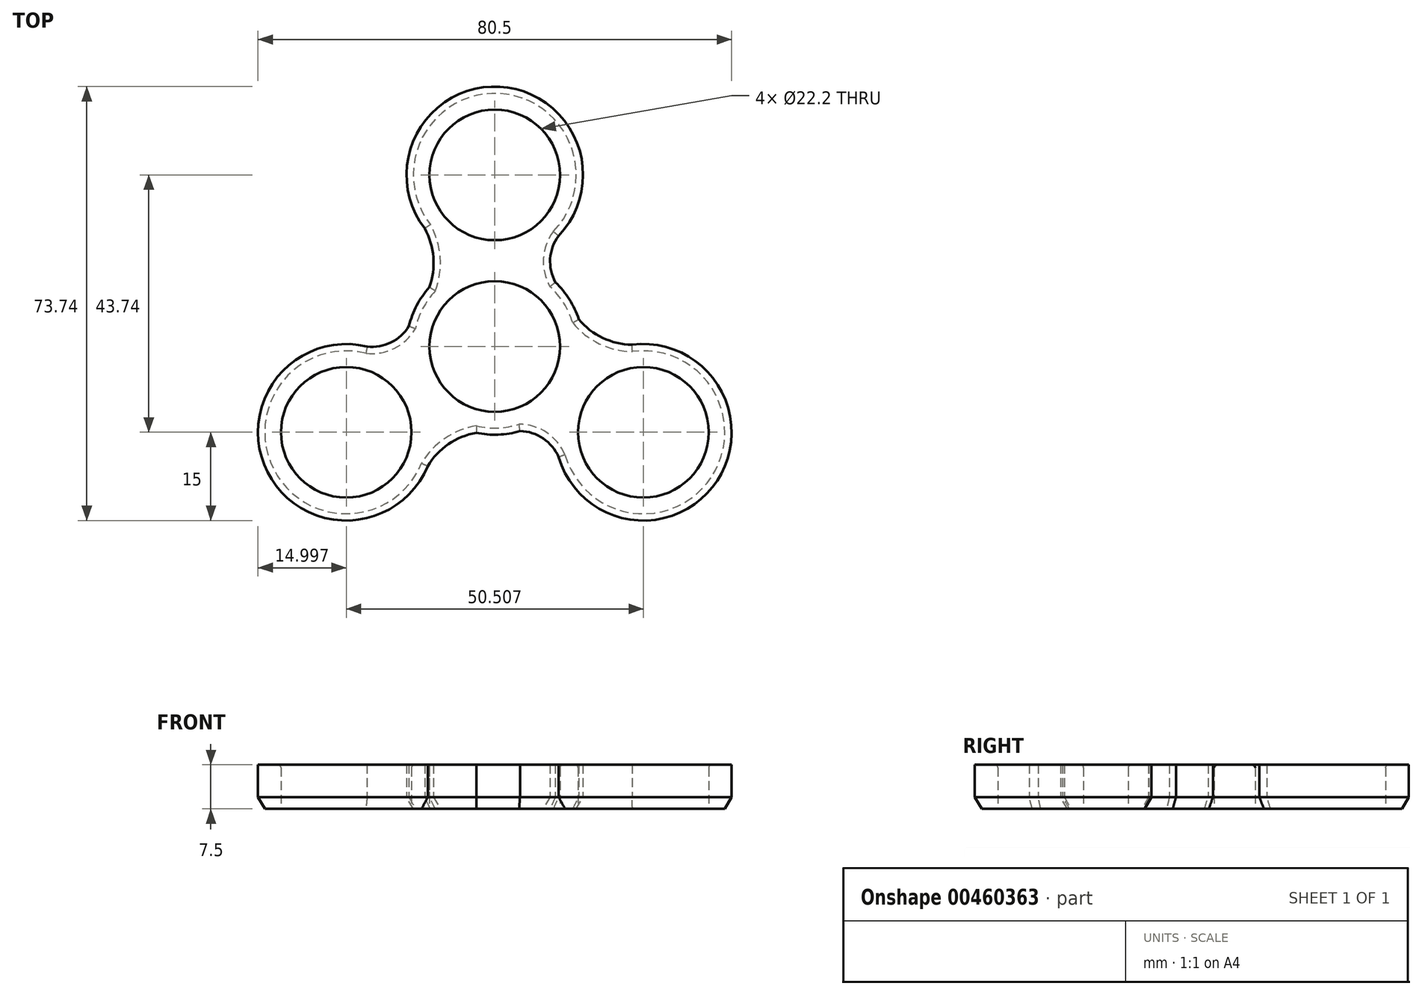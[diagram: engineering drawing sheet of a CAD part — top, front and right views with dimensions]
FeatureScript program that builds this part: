
annotation { "Feature Type Name" : "Feature", "Feature Type Description" : "" }
export const myFeature = defineFeature(function(context is Context, id is Id, definition is map)
    precondition{}
    {
        {
            var Q0;
            Q0=qCreatedBy(makeId("Top.planeOp"),FACE);
            var sketch = newSketch(context, id + "F0", { "sketchPlane" : qUnion([Q0])});
            skCircle(sketch, "E0", {"center": v(0, 0) * mm, "radius": 11.1 * mm});
            skCircle(sketch, "E1", {"center": v(0, 0) * mm, "radius": 15 * mm});
            skCircle(sketch, "E2", {"center": v(0, 29.16) * mm, "radius": 11.1 * mm});
            skCircle(sketch, "E3", {"center": v(0, 29.16) * mm, "radius": 15 * mm});
            skArc(sketch, "E4", {"start": v(-11.13, 10.06) * mm, "mid": v(-10.43, 15.14) * mm, "end": v(-11.92, 20.05) * mm});
            skArc(sketch, "E5", {"start": v(10.85, 18.8) * mm, "mid": v(9.41, 14.93) * mm, "end": v(10.3, 10.9) * mm});
            skCircle(sketch, "E6.1.0", {"center": v(-25.25, -14.58) * mm, "radius": 15 * mm});
            skCircle(sketch, "E6.1.1", {"center": v(-25.25, -14.58) * mm, "radius": 11.1 * mm});
            skArc(sketch, "E6.1.2", {"start": v(-3.15, -14.67) * mm, "mid": v(-7.9, -16.6) * mm, "end": v(-11.4, -20.35) * mm});
            skArc(sketch, "E6.1.3", {"start": v(-21.7, 0) * mm, "mid": v(-17.64, 0.69) * mm, "end": v(-14.6, 3.47) * mm});
            skCircle(sketch, "E6.2.0", {"center": v(25.25, -14.58) * mm, "radius": 15 * mm});
            skCircle(sketch, "E6.2.1", {"center": v(25.25, -14.58) * mm, "radius": 11.1 * mm});
            skArc(sketch, "E6.2.2", {"start": v(14.27, 4.6) * mm, "mid": v(18.33, 1.47) * mm, "end": v(23.33, 0.3) * mm});
            skArc(sketch, "E6.2.3", {"start": v(10.86, -18.8) * mm, "mid": v(8.22, -15.62) * mm, "end": v(4.29, -14.37) * mm});
            skSolve(sketch);
        }
        {
            var Q0;
            Q0 = qSketchRegion(id + "F0", true);
            extrude(context, id + "F1", {"entities" : qUnion([Q0]), "depth" : 7.5 * mm, "offsetDistance" : 25 * mm});
        }
        {
            var Q0;
            {var subQ0=sQuery(id+"F0.wireOp",EDGE,"E6.2.0");var subQ1=sQuery(id+"F0.wireOp",EDGE,"E1");var subQ2=makeQuery(id+"F0.imprint","INTERSECT",VERTEX,{"disambiguationData":[OD(0.0)],"derivedFrom":[subQ1,subQ0]});Q0=makeQuery(id+"F0.imprint","IMPRINT",FACE,{"disambiguationData":[TD([[makeQuery(id+"F0.imprint","IMPRINT",EDGE,{"disambiguationData":[TD([[subQ2,-1.0]])],"derivedFrom":subQ1}),1.0]])]});}
            var Q1;
            {var subQ0=sQuery(id+"F0.wireOp",EDGE,"E6.1.0");var subQ1=sQuery(id+"F0.wireOp",EDGE,"E1");var subQ2=makeQuery(id+"F0.imprint","INTERSECT",VERTEX,{"disambiguationData":[OD(0.0)],"derivedFrom":[subQ1,subQ0]});Q1=makeQuery(id+"F0.imprint","IMPRINT",FACE,{"disambiguationData":[TD([[makeQuery(id+"F0.imprint","IMPRINT",EDGE,{"disambiguationData":[TD([[subQ2,-1.0]])],"derivedFrom":subQ1}),1.0]])]});}
            var Q2;
            {var subQ0=sQuery(id+"F0.wireOp",EDGE,"E3");var subQ1=sQuery(id+"F0.wireOp",EDGE,"E1");var subQ2=makeQuery(id+"F0.imprint","INTERSECT",VERTEX,{"disambiguationData":[OD(0.0)],"derivedFrom":[subQ1,subQ0]});Q2=makeQuery(id+"F0.imprint","IMPRINT",FACE,{"disambiguationData":[TD([[makeQuery(id+"F0.imprint","IMPRINT",EDGE,{"disambiguationData":[TD([[subQ2,-1.0]])],"derivedFrom":subQ1}),1.0]])]});}
            extrude(context, id + "F2", {"entities" : qUnion([Q0, Q1, Q2]), "operationType" : NewBodyOperationType.ADD, "depth" : 7.5 * mm, "offsetDistance" : 25 * mm});
        }
        {
            var Q0;
            Q0=makeQuery(id+"F1.opExtrude","CAP_EDGE",EDGE,{"disambiguationData":[OSD([sQuery(id+"F0.wireOp",EDGE,"E2")])],"isStart":false});
            var Q1;
            Q1=makeQuery(id+"F1.opExtrude","CAP_EDGE",EDGE,{"disambiguationData":[OSD([sQuery(id+"F0.wireOp",EDGE,"E0")])],"isStart":false});
            var Q2;
            Q2=makeQuery(id+"F1.opExtrude","CAP_EDGE",EDGE,{"disambiguationData":[OSD([sQuery(id+"F0.wireOp",EDGE,"E6.2.1")])],"isStart":false});
            var Q3;
            Q3=makeQuery(id+"F1.opExtrude","CAP_EDGE",EDGE,{"disambiguationData":[OSD([sQuery(id+"F0.wireOp",EDGE,"E6.1.1")])],"isStart":false});
            fillet(context, id + "F3", {"entities" : qUnion([Q0, Q1, Q2, Q3]), "radius" : 0.5 * mm, "tangentPropagation" : true, "allowEdgeOverflow" : false});
        }
        {
            var Q0;
            {var subQ0=sQuery(id+"F0.wireOp",EDGE,"E6.1.0");Q0=makeQuery(id+"F1.opExtrude","CAP_EDGE",EDGE,{"disambiguationData":[OSD([subQ0]),TDD([makeQuery(id+"F0.imprint","IMPRINT",EDGE,{"disambiguationData":[TD([[makeQuery(id+"F0.imprint","INTERSECT",VERTEX,{"derivedFrom":[subQ0,sQuery(id+"F0.wireOp",EDGE,"E6.1.2")]}),1.0]])],"derivedFrom":subQ0})])],"isStart":true});}
            var Q1;
            Q1=makeQuery(id+"F1.opExtrude","CAP_EDGE",EDGE,{"disambiguationData":[OSD([sQuery(id+"F0.wireOp",EDGE,"E6.1.3")])],"isStart":true});
            var Q2;
            Q2=makeQuery(id+"F1.opExtrude","CAP_EDGE",EDGE,{"disambiguationData":[OSD([sQuery(id+"F0.wireOp",EDGE,"E6.1.2")])],"isStart":true});
            var Q3;
            Q3=makeQuery(id+"F1.opExtrude","CAP_EDGE",EDGE,{"disambiguationData":[OSD([sQuery(id+"F0.wireOp",EDGE,"E6.2.3")])],"isStart":true});
            var Q4;
            {var subQ0=sQuery(id+"F0.wireOp",EDGE,"E6.2.0");Q4=makeQuery(id+"F1.opExtrude","CAP_EDGE",EDGE,{"disambiguationData":[OSD([subQ0]),TDD([makeQuery(id+"F0.imprint","IMPRINT",EDGE,{"disambiguationData":[TD([[makeQuery(id+"F0.imprint","INTERSECT",VERTEX,{"derivedFrom":[subQ0,sQuery(id+"F0.wireOp",EDGE,"E6.2.2")]}),1.0]])],"derivedFrom":subQ0})])],"isStart":true});}
            var Q5;
            Q5=makeQuery(id+"F1.opExtrude","CAP_EDGE",EDGE,{"disambiguationData":[OSD([sQuery(id+"F0.wireOp",EDGE,"E6.2.2")])],"isStart":true});
            var Q6;
            Q6=makeQuery(id+"F1.opExtrude","CAP_EDGE",EDGE,{"disambiguationData":[OSD([sQuery(id+"F0.wireOp",EDGE,"E5")])],"isStart":true});
            var Q7;
            {var subQ0=sQuery(id+"F0.wireOp",EDGE,"E3");Q7=makeQuery(id+"F1.opExtrude","CAP_EDGE",EDGE,{"disambiguationData":[OSD([subQ0]),TDD([makeQuery(id+"F0.imprint","IMPRINT",EDGE,{"disambiguationData":[TD([[makeQuery(id+"F0.imprint","INTERSECT",VERTEX,{"derivedFrom":[subQ0,sQuery(id+"F0.wireOp",EDGE,"E4")]}),1.0]])],"derivedFrom":subQ0})])],"isStart":true});}
            var Q8;
            Q8=makeQuery(id+"F1.opExtrude","CAP_EDGE",EDGE,{"disambiguationData":[OSD([sQuery(id+"F0.wireOp",EDGE,"E4")])],"isStart":true});
            var Q9;
            {var subQ0=sQuery(id+"F0.wireOp",EDGE,"E1");Q9=makeQuery(id+"F1.opExtrude","CAP_EDGE",EDGE,{"disambiguationData":[OSD([subQ0]),TDD([makeQuery(id+"F0.imprint","IMPRINT",EDGE,{"disambiguationData":[TD([[makeQuery(id+"F0.imprint","INTERSECT",VERTEX,{"derivedFrom":[subQ0,sQuery(id+"F0.wireOp",EDGE,"E5")]}),1.0]])],"derivedFrom":subQ0})])],"isStart":true});}
            var Q10;
            {var subQ0=sQuery(id+"F0.wireOp",EDGE,"E1");Q10=makeQuery(id+"F1.opExtrude","CAP_EDGE",EDGE,{"disambiguationData":[OSD([subQ0]),TDD([makeQuery(id+"F0.imprint","IMPRINT",EDGE,{"disambiguationData":[TD([[makeQuery(id+"F0.imprint","INTERSECT",VERTEX,{"derivedFrom":[subQ0,sQuery(id+"F0.wireOp",EDGE,"E4")]}),-1.0]])],"derivedFrom":subQ0})])],"isStart":true});}
            var Q11;
            {var subQ0=sQuery(id+"F0.wireOp",EDGE,"E1");Q11=makeQuery(id+"F1.opExtrude","CAP_EDGE",EDGE,{"disambiguationData":[OSD([subQ0]),TDD([makeQuery(id+"F0.imprint","IMPRINT",EDGE,{"disambiguationData":[TD([[makeQuery(id+"F0.imprint","INTERSECT",VERTEX,{"derivedFrom":[subQ0,sQuery(id+"F0.wireOp",EDGE,"E6.1.2")]}),-1.0]])],"derivedFrom":subQ0})])],"isStart":true});}
            chamfer(context, id + "F4", {"entities" : qUnion([Q0, Q1, Q2, Q3, Q4, Q5, Q6, Q7, Q8, Q9, Q10, Q11]), "chamferType" : ChamferType.OFFSET_ANGLE, "width" : 2 * mm, "oppositeDirection" : false, "angle" : 30 * degree, "tangentPropagation" : true});
        }
    });
